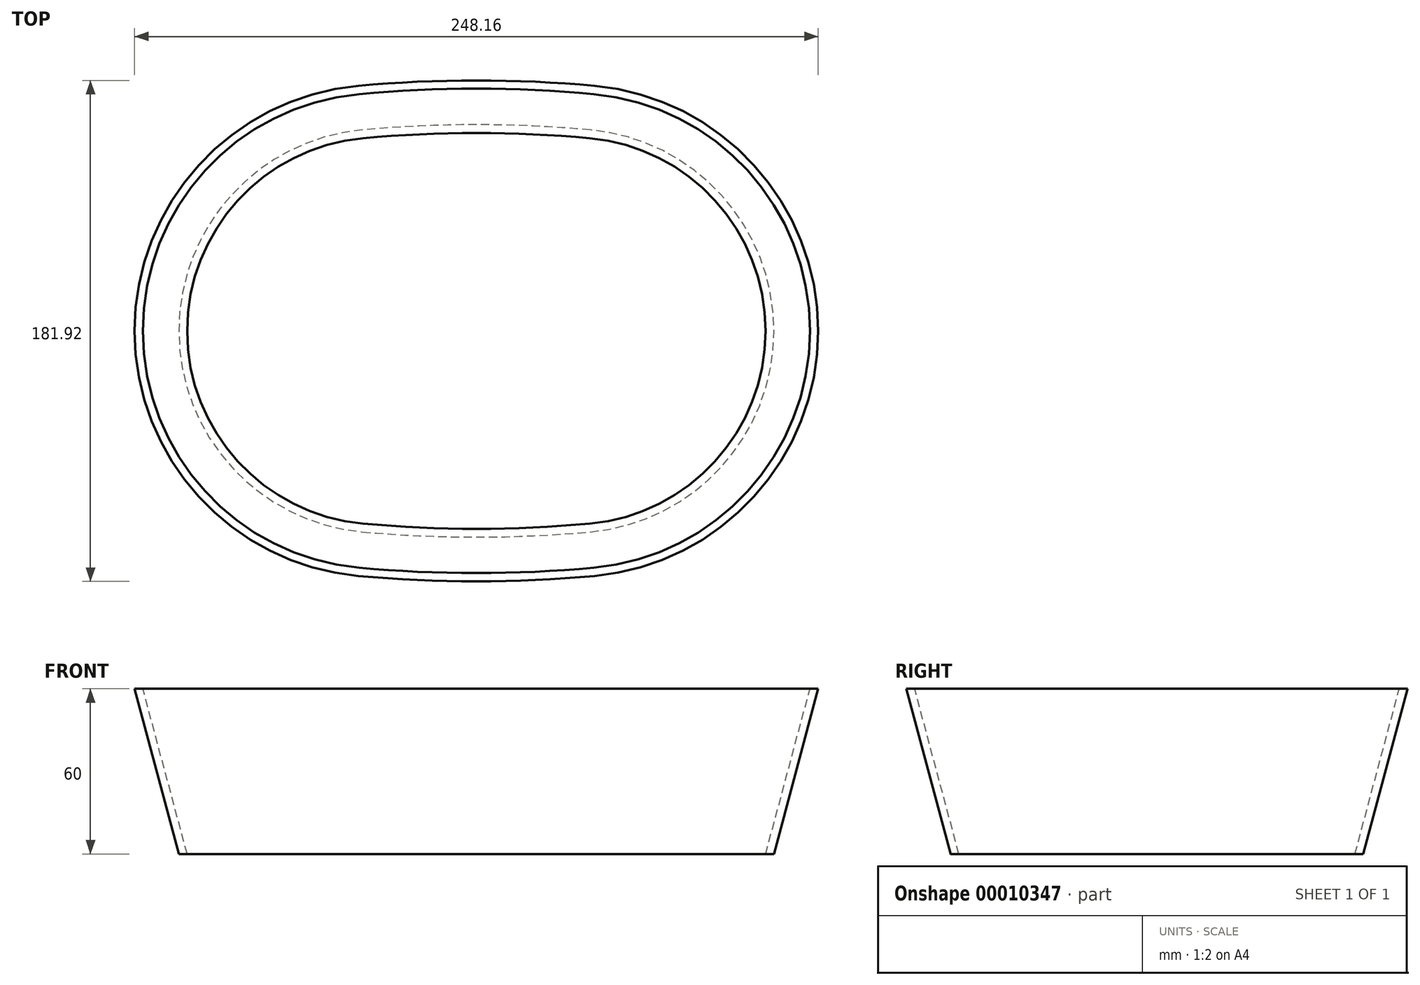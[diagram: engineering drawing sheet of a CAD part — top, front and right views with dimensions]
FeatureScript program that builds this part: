
annotation { "Feature Type Name" : "Feature", "Feature Type Description" : "" }
export const myFeature = defineFeature(function(context is Context, id is Id, definition is map)
    precondition{}
    {
        {
            var Q0;
            Q0=qCreatedBy(makeId("Top.planeOp"),FACE);
            var sketch = newSketch(context, id + "F0", { "sketchPlane" : qUnion([Q0])});
            skPoint(sketch, "E0.rect.middle", {"position": v(0, 0) * mm});
            skArc(sketch, "E1", {"start": v(-41.13, 70) * mm, "mid": v(-105, 0) * mm, "end": v(-41.13, -70) * mm});
            skLineSegment(sketch, "E2", {"start": v(0, 0) * mm, "end": v(-34.7, 0) * mm, "construction": true});
            skArc(sketch, "E3", {"start": v(41.13, 70) * mm, "mid": v(0, 71.88) * mm, "end": v(-41.13, 70) * mm});
            skLineSegment(sketch, "E4", {"start": v(0, -378.12) * mm, "end": v(0, 0) * mm, "construction": true});
            skLineSegment(sketch, "E5.rect.bottom", {"start": v(41.13, -70) * mm, "end": v(-41.13, -70) * mm, "construction": true});
            skLineSegment(sketch, "E5.rect.top", {"start": v(41.13, 70) * mm, "end": v(-41.13, 70) * mm, "construction": true});
            skArc(sketch, "E6", {"start": v(-41.13, -70) * mm, "mid": v(0, -71.88) * mm, "end": v(41.13, -70) * mm});
            skLineSegment(sketch, "E7", {"start": v(-105, 0) * mm, "end": v(105, 0) * mm, "construction": true});
            skArc(sketch, "E8", {"start": v(105, 0) * mm, "mid": v(86.63, 47.38) * mm, "end": v(41.13, 70) * mm});
            skArc(sketch, "E9", {"start": v(41.13, -70) * mm, "mid": v(86.63, -47.38) * mm, "end": v(105, 0) * mm});
            skSolve(sketch);
        }
        {
            var Q0;
            Q0=qCreatedBy(makeId("Front.planeOp"),FACE);
            var sketch = newSketch(context, id + "F1", { "sketchPlane" : qUnion([Q0])});
            skLineSegment(sketch, "E10", {"start": v(105, 0) * mm, "end": v(121.08, 60) * mm});
            skLineSegment(sketch, "E11", {"start": v(121.08, 60) * mm, "end": v(124.08, 60) * mm});
            skLineSegment(sketch, "E12", {"start": v(124.08, 60) * mm, "end": v(108, 0) * mm});
            skLineSegment(sketch, "E13", {"start": v(108, 0) * mm, "end": v(105, 0) * mm});
            skSolve(sketch);
        }
        {
            var Q0;
            Q0=qSketchRegion(id+"F1",true);
            var Q1;
            Q1=sQuery(id+"F0.wireOp",EDGE,"E8");
            var Q2;
            Q2=sQuery(id+"F0.wireOp",EDGE,"E3");
            var Q3;
            Q3=sQuery(id+"F0.wireOp",EDGE,"E1");
            var Q4;
            Q4=sQuery(id+"F0.wireOp",EDGE,"E6");
            var Q5;
            Q5=sQuery(id+"F0.wireOp",EDGE,"E9");
            sweep(context, id + "F2", {"profiles" : qUnion([Q0]), "path" : qUnion([Q1, Q2, Q3, Q4, Q5])});
        }
    });
